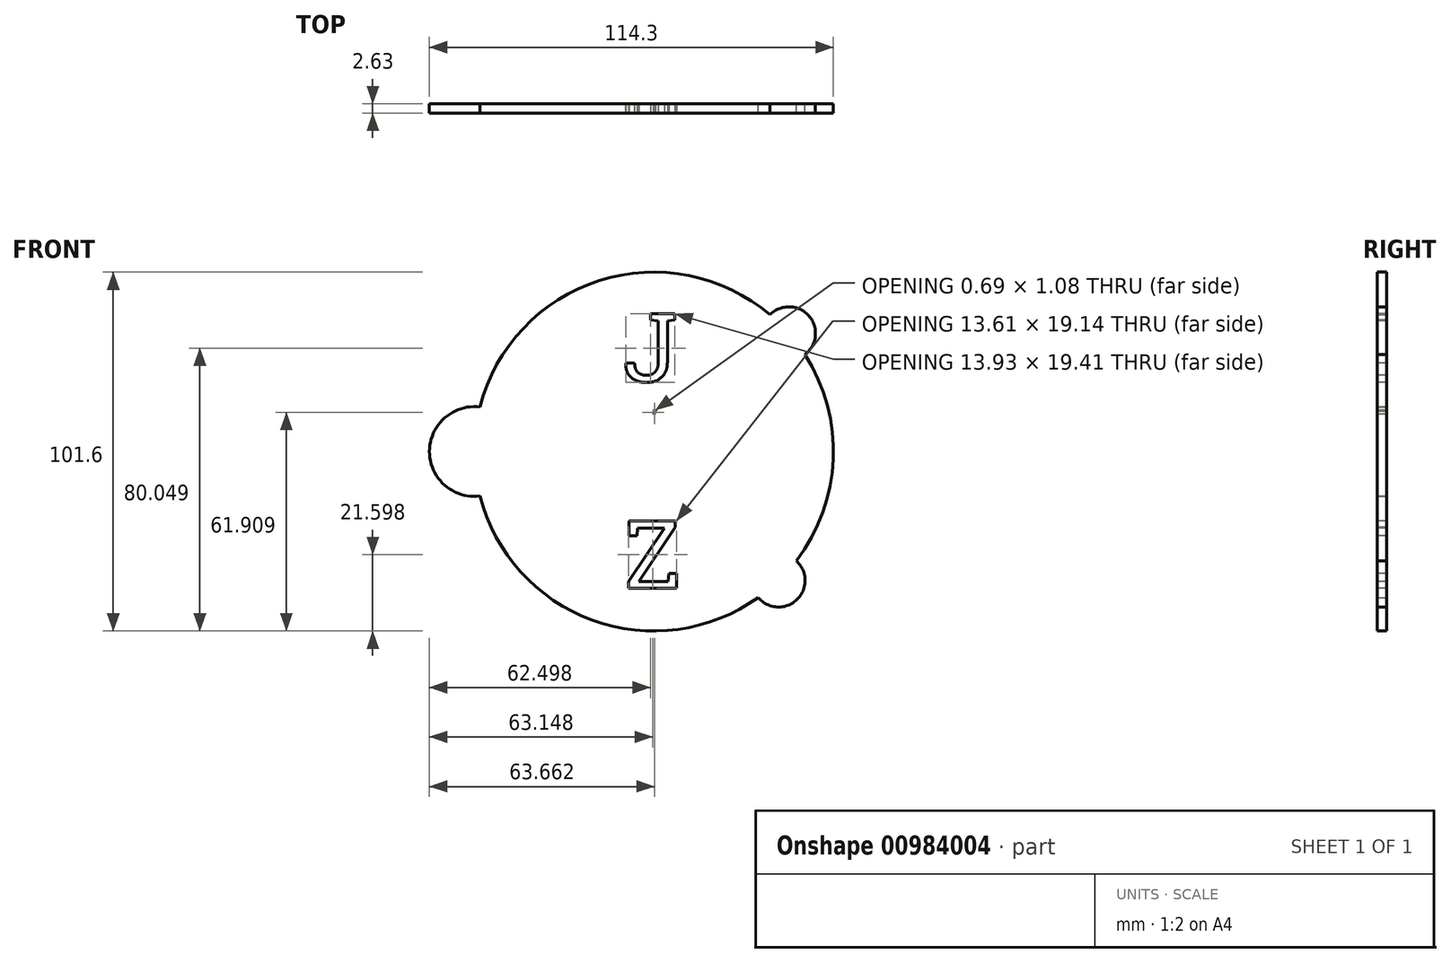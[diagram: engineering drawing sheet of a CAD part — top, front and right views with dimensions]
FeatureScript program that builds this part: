
annotation { "Feature Type Name" : "Feature", "Feature Type Description" : "" }
export const myFeature = defineFeature(function(context is Context, id is Id, definition is map)
    precondition{}
    {
        {
            var Q0;
            Q0=qCreatedBy(makeId("Front.planeOp"),FACE);
            var sketch = newSketch(context, id + "F0", { "sketchPlane" : qUnion([Q0])});
            skArc(sketch, "E0", {"start": v(-49.21, -12.6) * mm, "mid": v(-17.42, -47.72) * mm, "end": v(29.53, -41.34) * mm});
            skArc(sketch, "E1", {"start": v(-49.21, 12.6) * mm, "mid": v(-63.5, 0) * mm, "end": v(-49.21, -12.6) * mm});
            skArc(sketch, "E2", {"start": v(42.73, 27.47) * mm, "mid": v(43.87, 38.4) * mm, "end": v(32.88, 38.72) * mm});
            skArc(sketch, "E3", {"start": v(29.53, -41.34) * mm, "mid": v(40.5, -41.93) * mm, "end": v(40.29, -30.94) * mm});
            skArc(sketch, "E4.trimOffspring", {"start": v(32.88, 38.72) * mm, "mid": v(-15.4, 48.4) * mm, "end": v(-49.21, 12.6) * mm});
            skArc(sketch, "E5.trimOffspring", {"start": v(40.29, -30.94) * mm, "mid": v(50.76, -2.12) * mm, "end": v(42.73, 27.47) * mm});
            skSolve(sketch);
        }
        {
            var Q0;
            Q0 = qSketchRegion(id + "F0", true);
            extrude(context, id + "F1", {"entities" : qUnion([Q0]), "depth" : 2.62 * mm, "offsetDistance" : 25 * mm});
        }
        {
            var Q0;
            Q0=makeQuery(id+"F1.opExtrude","CAP_FACE",FACE,{"disambiguationData":[OSD([sQuery(id+"F0.wireOp",EDGE,"E0"),sQuery(id+"F0.wireOp",EDGE,"E1")])],"isStart":false});
            var sketch = newSketch(context, id + "F2", { "sketchPlane" : qUnion([Q0])});
            skText(sketch, "E6", { "text": "J", "fontName": "RobotoSlab-Regular.ttf"});
            skText(sketch, "E7", { "text": "Z", "fontName": "RobotoSlab-Regular.ttf"});
            const initialGuessF2  = {"E6": [-0.00881, 0.01982, 1, 0, 0.01938], "E7": [-0.00837, -0.03877, 1, 0, 0.01938]};
            skSetInitialGuess(sketch, initialGuessF2);
            skSolve(sketch);
        }
        {
            var Q0;
            Q0 = qSketchRegion(id + "F2", true);
            extrude(context, id + "F3", {"entities" : qUnion([Q0]), "operationType" : NewBodyOperationType.REMOVE, "endBound" : BoundingType.UP_TO_NEXT, "oppositeDirection" : true, "depth" : 25 * mm, "offsetDistance" : 25 * mm});
        }
        {
            var Q0;
            Q0=makeQuery(id+"F1.opExtrude","CAP_FACE",FACE,{"disambiguationData":[OSD([sQuery(id+"F0.wireOp",EDGE,"E0"),sQuery(id+"F0.wireOp",EDGE,"E1")])],"isStart":false});
            var sketch = newSketch(context, id + "F4", { "sketchPlane" : qUnion([Q0])});
            skLineSegment(sketch, "E8", {"start": v(-0.2, 11.38) * mm, "end": v(0.02, 10.57) * mm});
            skLineSegment(sketch, "E9", {"start": v(0.02, 10.57) * mm, "end": v(0.5, 11.65) * mm});
            skLineSegment(sketch, "E10", {"start": v(0.5, 11.65) * mm, "end": v(-0.19, 11.35) * mm});
            skFitSpline(sketch, "E11", {"points": [v(-1.17, -11.01) * mm, v(-1.86, -10.24) * mm, v(-3.58, -8.73) * mm, v(-5, -7.67) * mm]});
            skFitSpline(sketch, "E12", {"points": [v(-5, -7.67) * mm, v(-9.19, -4.5) * mm, v(-9.76, -4.04) * mm, v(-11.46, -2.48) * mm]});
            skFitSpline(sketch, "E13", {"points": [v(-11.46, -2.48) * mm, v(-14.6, 0.41) * mm, v(-15.93, 3.32) * mm, v(-15.92, 7.25) * mm]});
            skFitSpline(sketch, "E14", {"points": [v(-15.92, 7.25) * mm, v(-15.92, 9.17) * mm, v(-15.79, 9.91) * mm, v(-15.25, 11.04) * mm]});
            skFitSpline(sketch, "E15", {"points": [v(-15.25, 11.04) * mm, v(-14.34, 12.97) * mm, v(-13, 14.4) * mm, v(-11.28, 15.27) * mm]});
            skFitSpline(sketch, "E16", {"points": [v(-11.28, 15.27) * mm, v(-10.06, 15.89) * mm, v(-9.46, 16.16) * mm, v(-7.42, 16.17) * mm]});
            skFitSpline(sketch, "E17", {"points": [v(-7.42, 16.17) * mm, v(-5.3, 16.18) * mm, v(-4.85, 15.94) * mm, v(-3.6, 15.25) * mm]});
            skFitSpline(sketch, "E18", {"points": [v(-3.6, 15.25) * mm, v(-2.08, 14.41) * mm, v(-0.5, 12.62) * mm, v(-0.19, 11.35) * mm]});
            skFitSpline(sketch, "E19", {"points": [v(0.5, 11.65) * mm, v(3.3, 17.75) * mm, v(12.2, 17.66) * mm, v(15.3, 11.5) * mm]});
            skFitSpline(sketch, "E20", {"points": [v(15.3, 11.5) * mm, v(16.28, 9.54) * mm, v(16.39, 5.37) * mm, v(15.52, 3.01) * mm]});
            skFitSpline(sketch, "E21", {"points": [v(15.52, 3.01) * mm, v(14.38, -0.05) * mm, v(12.25, -2.4) * mm, v(7.3, -5.98) * mm]});
            skFitSpline(sketch, "E22", {"points": [v(7.3, -5.98) * mm, v(4.07, -8.33) * mm, v(0.4, -11.89) * mm, v(0.15, -12.39) * mm]});
            skFitSpline(sketch, "E23", {"points": [v(0.15, -12.39) * mm, v(-0.14, -12.97) * mm, v(0.14, -12.48) * mm, v(-1.17, -11.01) * mm]});
            skSolve(sketch);
        }
        {
            var Q0;
            Q0 = qSketchRegion(id + "F4", true);
            extrude(context, id + "F5", {"entities" : qUnion([Q0]), "operationType" : NewBodyOperationType.REMOVE, "endBound" : BoundingType.UP_TO_NEXT, "oppositeDirection" : true, "depth" : 25 * mm, "offsetDistance" : 25 * mm});
        }
    });
